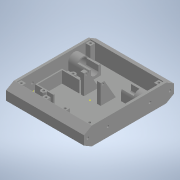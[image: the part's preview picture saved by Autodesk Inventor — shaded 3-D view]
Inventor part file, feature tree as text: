
AUTODESK INVENTOR PART (.ipt)
format: ipt  version: 2020 (Build 240168000, 168)  size: 532,480 bytes
history: native  units: in
note: dims shown in document units (in); Inventor stores cm internally (conversion verified against a paired STEP export)
features: extrude x14, sketch x14, projected_geometry x14, mirror x4, plane x1
ambient origin geometry x8: Origin, YZ Plane, XZ Plane, XY Plane, X Axis, Y Axis, Z Axis, Center Point
bodies: Solid1 (feature_tree)
feature tree (47):
  extrude  "Extrusion1"  Depth=5.9055in
  extrude  "Extrusion2"  TaperAngle=0.0deg  [1 undecoded]
  extrude  "Extrusion3"  Depth=1.063in
  extrude  "Extrusion4"  Depth=0.315in
  extrude  "Extrusion5"  TaperAngle=0.0deg  [1 undecoded]
  extrude  "Extrusion6"  Depth=0.5906in
  mirror  "Mirror1"
  extrude  "Extrusion7"  Depth=0.0787in
  mirror  "Mirror2"
  extrude  "Extrusion8"  Depth=0.6102in
  mirror  "Mirror3"
  plane  "Work Plane1"
  extrude  "Extrusion9"  Depth=0.7874in TaperAngle=0.0deg
  mirror  "Mirror4"
  extrude  "Extrusion10"  Depth=6.063in TaperAngle=0.0deg
  extrude  "Extrusion11"  Depth=0.1575in
  extrude  "Extrusion12"  TaperAngle=0.0deg  [1 undecoded]
  extrude  "Extrusion13"  Depth=0.2756in
  extrude  "Extrusion14"  Depth=0.4331in
  sketch  "Sketch19"  dims[d32=0.0in d33=0.4331in d34=0.122in d38=2.7559in d40=0.061in d41=0.0909in d42=0.2362in d43=0.0in d44=60.0deg d45=0.0787in d46=0.315in d48=0.993in d49=0.0in d53=0.2756in d54=0.0in d55=0.4724in d56=1.2008in d57=1.6142in d58=1.5945in d59=0.0787in d60=0.0787in d62=0.315in d63=0.7677in d64=0.0in d66=0.1476in d67=0.2756in d68=0.0in d69=0.8268in d70=0.2953in d71=0.0394in d72=0.0in d89=0.0157in d90=0.0157in d91=0.1476in d92=0.1476in]
  sketch  "Sketch1"  dims[d0=1.1811in d1=5.9055in]
  sketch  "Sketch2"  dims[d2=5.1181in d3=0.0in]
  projected_geometry  "Projected Loop1"
  sketch  "Sketch3"  dims[d4=0.1575in d5=1.063in]
  projected_geometry  "Projected Loop2"
  projected_geometry  "Projected Loop3"
  sketch  "Sketch4"  dims[d6=0.0in d8=0.315in]
  projected_geometry  "Projected Loop4"
  sketch  "Sketch6"  dims[d10=0.993in d11=0.0in]
  sketch  "Sketch7"  dims[d12=0.6496in d13=0.5906in]
  sketch  "Sketch9"  dims[d14=1.5748in d15=0.0787in]
  sketch  "Sketch10"  dims[d16=0.5512in d17=0.0in d18=0.6102in]
  sketch  "Sketch12"  dims[d19=0.4803in d20=0.7874in d21=0.0in]
  projected_geometry  "Projected Loop6"
  projected_geometry  "Projected Loop7"
  projected_geometry  "Projected Loop8"
  sketch  "Sketch13"  dims[d22=0.1654in d23=6.063in d24=0.0in]
  sketch  "Sketch14"  dims[d25=0.5114in d26=0.1575in]
  sketch  "Sketch15"  dims[d27=1.5748in d28=0.0in d29=0.0in]
  projected_geometry  "Projected Loop15"
  sketch  "Sketch16"  dims[d30=0.1575in d31=0.2756in]
  projected_geometry  "Projected Loop19"
  projected_geometry  "Projected Loop20"
  projected_geometry  "Projected Loop21"
  projected_geometry  "Projected Loop22"
  projected_geometry  "Projected Loop23"
  projected_geometry  "Projected Loop24"
note: 3 required parameter values undecoded (feature->parameter linkage not recoverable at this tier; creation-order binding heuristic only, values carry confidence <= 0.55)
